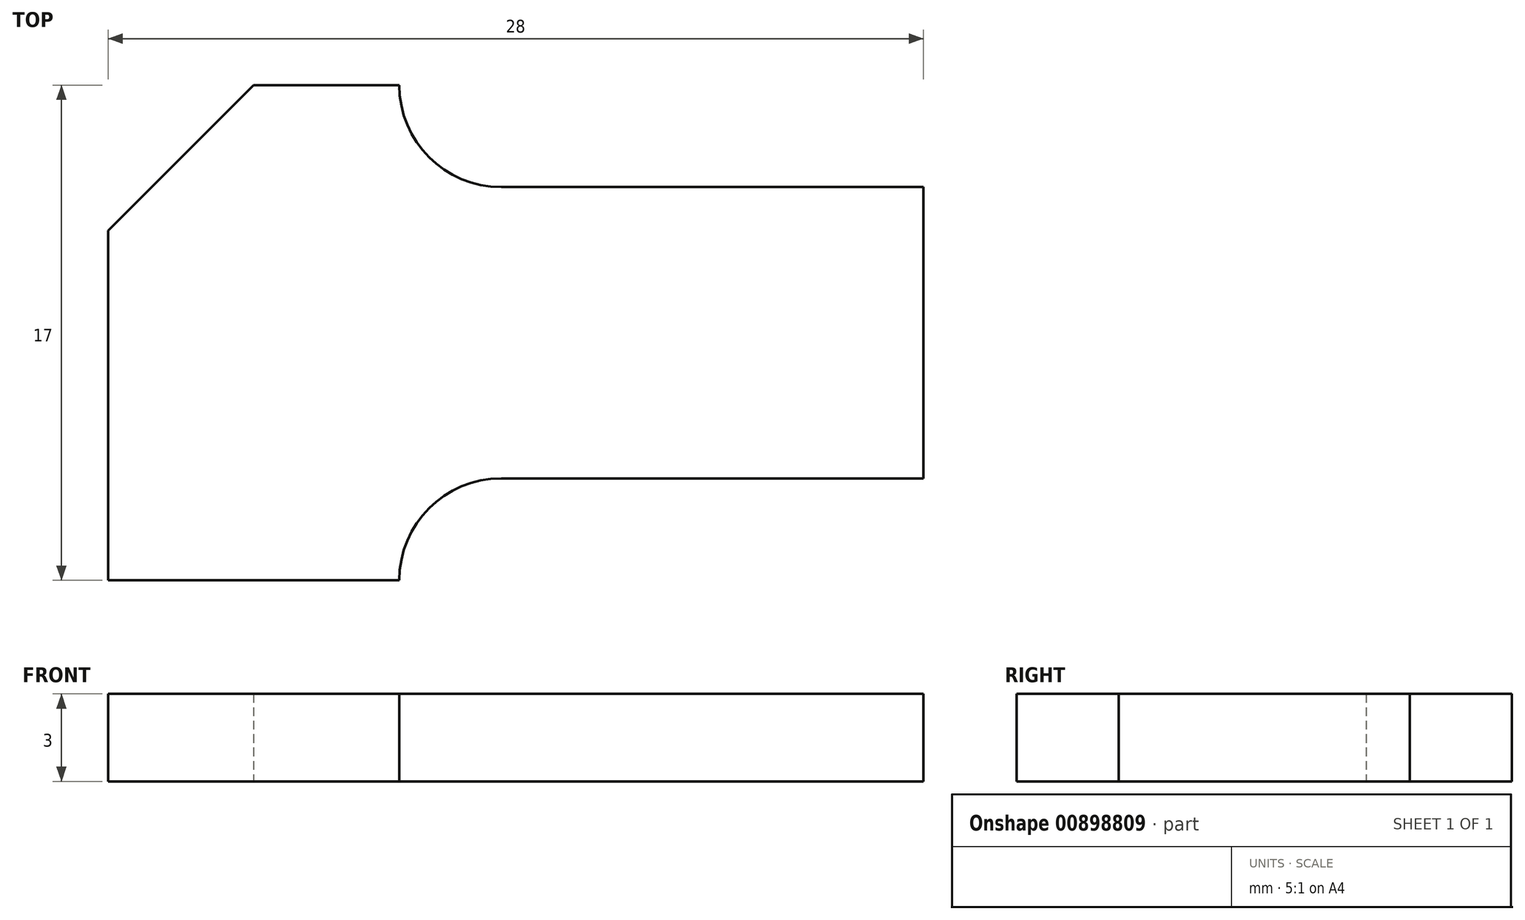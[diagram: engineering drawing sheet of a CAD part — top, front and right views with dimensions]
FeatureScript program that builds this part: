
annotation { "Feature Type Name" : "Feature", "Feature Type Description" : "" }
export const myFeature = defineFeature(function(context is Context, id is Id, definition is map)
    precondition{}
    {
        {
            var Q0;
            Q0=qCreatedBy(makeId("Top.planeOp"),FACE);
            var sketch = newSketch(context, id + "F0", { "sketchPlane" : qUnion([Q0])});
            skLineSegment(sketch, "E0", {"start": v(0, 0) * mm, "end": v(0, 12) * mm});
            skLineSegment(sketch, "E1", {"start": v(5, 17) * mm, "end": v(10, 17) * mm});
            skLineSegment(sketch, "E2", {"start": v(10, 17) * mm, "end": v(10, 13.5) * mm});
            skLineSegment(sketch, "E3", {"start": v(10, 13.5) * mm, "end": v(28, 13.5) * mm});
            skLineSegment(sketch, "E4", {"start": v(28, 13.5) * mm, "end": v(28, 3.5) * mm});
            skLineSegment(sketch, "E5", {"start": v(28, 3.5) * mm, "end": v(10, 3.5) * mm});
            skLineSegment(sketch, "E6", {"start": v(10, 3.5) * mm, "end": v(10, 0) * mm});
            skLineSegment(sketch, "E7", {"start": v(10, 0) * mm, "end": v(0, 0) * mm});
            skLineSegment(sketch, "E8", {"start": v(5, 17) * mm, "end": v(0, 12) * mm});
            skPoint(sketch, "E9.orphan", {"position": v(0, 17) * mm});
            skSolve(sketch);
        }
        {
            var Q0;
            Q0 = qSketchRegion(id + "F0", true);
            extrude(context, id + "F1", {"entities" : qUnion([Q0]), "depth" : 3 * mm, "offsetDistance" : 25 * mm});
        }
        {
            var Q0;
            Q0=makeQuery(id+"F1.opExtrude","SWEPT_EDGE",EDGE,{"disambiguationData":[OSD([sQuery(id+"F0.wireOp",EDGE,"E2"),sQuery(id+"F0.wireOp",EDGE,"E3")])]});
            fillet(context, id + "F2", {"entities" : qUnion([Q0]), "radius" : 3.5 * mm, "tangentPropagation" : true, "allowEdgeOverflow" : false});
        }
        {
            var Q0;
            Q0=makeQuery(id+"F1.opExtrude","SWEPT_EDGE",EDGE,{"disambiguationData":[OSD([sQuery(id+"F0.wireOp",EDGE,"E5"),sQuery(id+"F0.wireOp",EDGE,"E6")])]});
            fillet(context, id + "F3", {"entities" : qUnion([Q0]), "radius" : 3.5 * mm, "tangentPropagation" : true, "allowEdgeOverflow" : false});
        }
    });
